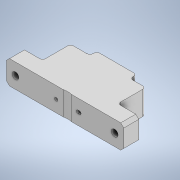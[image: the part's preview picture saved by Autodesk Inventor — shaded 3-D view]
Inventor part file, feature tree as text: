
AUTODESK INVENTOR PART (.ipt)
format: ipt  version: 2020 (Build 240168000, 168)  size: 273,920 bytes
history: native  units: in
note: dims shown in document units (in); Inventor stores cm internally (conversion verified against a paired STEP export)
features: sketch x7, extrude x5, hole x4, fillet x3, chamfer x1
ambient origin geometry x8: Origin, YZ Plane, XZ Plane, XY Plane, X Axis, Y Axis, Z Axis, Center Point
bodies: Solid1 (feature_tree)
feature tree (20):
  extrude  "Extrusion1"  Depth=3.0699in
  sketch  "Sketch2"  dims[d3=1.5349in d4=0.0in]
  hole  "Hole1"  [1 undecoded]
  hole  "Hole3"  [1 undecoded]
  extrude  "Extrusion2"  Depth=0.4724in
  fillet  "Fillet1"  Radius=0.4724in
  fillet  "Fillet2"  Radius=0.2362in
  extrude  "Extrusion3"  Depth=0.62in
  chamfer  "Chamfer1"  Distance=0.51in
  fillet  "Fillet4"  Radius=0.537in
  extrude  "Extrusion4"  Depth=0.4843in
  hole  "Hole4"  [1 undecoded]
  extrude  "Extrusion6"  Depth=0.4843in
  hole  "Hole5"  [1 undecoded]
  sketch  "Sketch1"  dims[d0=1.3034in d1=0.0in d2=3.0699in]
  sketch  "Sketch4"  dims[d5=0.0in d6=0.62in]
  sketch  "Sketch5"  dims[d7=0.31in d8=0.4724in d9=0.4724in d14=0.2362in]
  sketch  "Sketch6"  dims[d15=0.62in d16=0.31in]
  sketch  "Sketch8"  dims[d17=0.2362in]
  sketch  "Sketch9"  dims[d18=0.31in d19=0.51in d20=0.537in d21=0.1772in d22=0.328in d23=0.315in d24=1.1854in d25=0.5635in d26=1.3035in d27=0.0in d48=0.0in d49=0.0in d50=0.4724in d51=0.4724in d54=0.2362in d55=0.62in d56=0.31in d57=0.2362in d58=0.31in d59=0.537in d60=0.51in d61=1.0in d62=0.1772in d63=0.328in d64=0.3126in d65=1.1854in d66=0.5635in d67=0.4843in d68=0.0in d69=0.1775in d70=0.0in d72=1.0in d73=0.0787in d74=0.31in d75=0.313in d76=0.0787in d77=0.9098in d78=0.0in d80=0.0787in d81=0.0787in d82=45.0deg d83=0.0787in d84=0.0787in d85=0.0787in d86=1.0in d87=0.4862in d88=0.0in d89=0.0in d90=0.0in d91=0.2165in d92=0.0in d93=0.2953in d94=0.0in d95=0.2953in d96=0.0413in d97=0.0392in d98=0.537in d99=0.31in d100=0.0827in d101=0.328in d102=0.3126in d103=1.1854in d104=0.5635in d105=0.0827in d106=0.0in d121=0.0in d122=0.2165in d123=0.0in d124=0.2953in d125=0.0in d126=0.2953in d127=0.0413in d128=0.0392in d129=0.537in d131=0.537in d132=0.313in d133=0.0827in d134=0.0in d135=0.0in d136=0.0in d137=0.4724in d138=0.4724in d139=0.2362in d140=0.62in d141=0.31in d142=0.2362in d143=0.31in d144=0.51in d145=0.537in d146=1.0in d147=0.313in d148=0.0787in d149=0.0787in d150=0.13in d151=0.328in d152=0.3126in d153=1.1854in d154=0.5635in d155=0.4843in d156=0.0in d157=0.31in d158=0.8108in d159=0.0025in d160=0.0295in d161=0.0148in]
note: 4 required parameter values undecoded (feature->parameter linkage not recoverable at this tier; creation-order binding heuristic only, values carry confidence <= 0.55)
